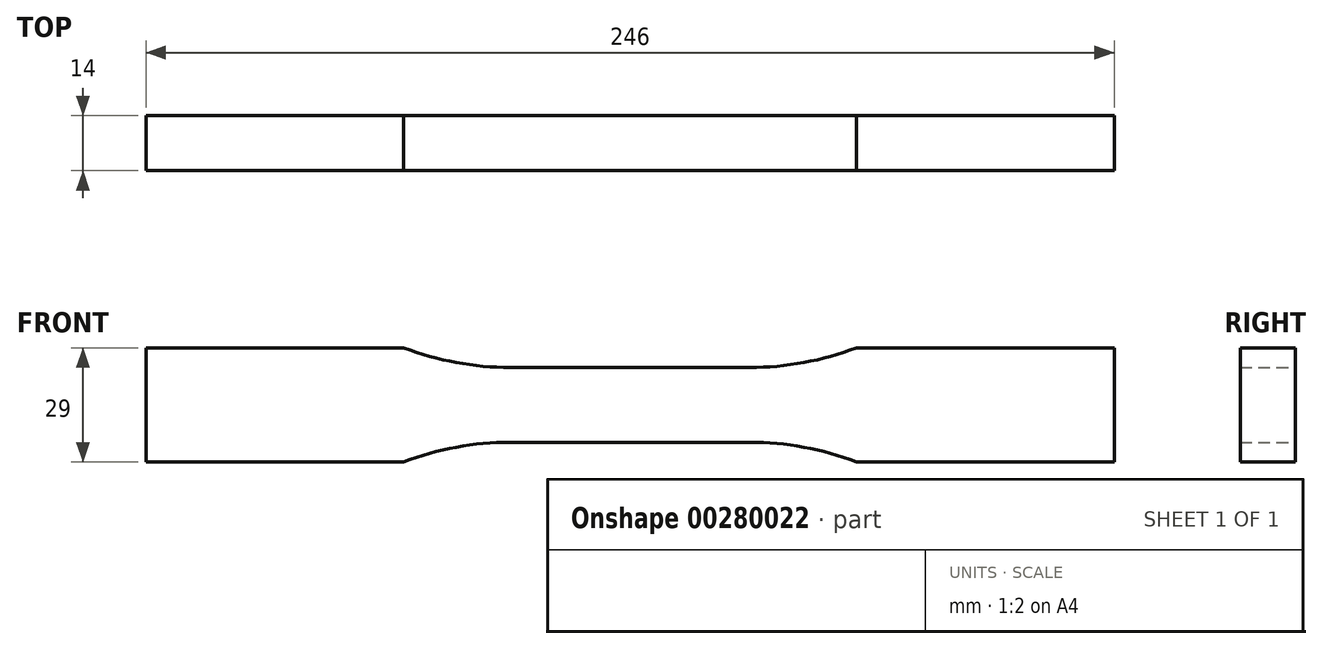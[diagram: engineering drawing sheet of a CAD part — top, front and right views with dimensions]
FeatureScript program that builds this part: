
annotation { "Feature Type Name" : "Feature", "Feature Type Description" : "" }
export const myFeature = defineFeature(function(context is Context, id is Id, definition is map)
    precondition{}
    {
        {
            var Q0;
            Q0=qCreatedBy(makeId("Front.planeOp"),FACE);
            var sketch = newSketch(context, id + "F0", { "sketchPlane" : qUnion([Q0])});
            skLineSegment(sketch, "E0", {"start": v(0, 9.5) * mm, "end": v(30.39, 9.5) * mm});
            skArc(sketch, "E1", {"start": v(30.39, 9.5) * mm, "mid": v(44.17, 10.76) * mm, "end": v(57.5, 14.5) * mm});
            skLineSegment(sketch, "E2", {"start": v(57.5, 14.5) * mm, "end": v(123, 14.5) * mm});
            skLineSegment(sketch, "E3", {"start": v(123, 14.5) * mm, "end": v(123, 0) * mm});
            skLineSegment(sketch, "E4.MirrorCS", {"start": v(0, -9.5) * mm, "end": v(30.39, -9.5) * mm});
            skLineSegment(sketch, "E5.MirrorCS", {"start": v(123, -14.5) * mm, "end": v(123, 0) * mm});
            skLineSegment(sketch, "E6.MirrorCS", {"start": v(57.5, -14.5) * mm, "end": v(123, -14.5) * mm});
            skArc(sketch, "E7.MirrorCS", {"start": v(30.39, -9.5) * mm, "mid": v(44.17, -10.76) * mm, "end": v(57.5, -14.5) * mm});
            skArc(sketch, "E8.MirrorCS", {"start": v(-30.39, -9.5) * mm, "mid": v(-44.17, -10.76) * mm, "end": v(-57.5, -14.5) * mm});
            skLineSegment(sketch, "E9.MirrorCS", {"start": v(-57.5, -14.5) * mm, "end": v(-123, -14.5) * mm});
            skArc(sketch, "E10.MirrorCS", {"start": v(-30.39, 9.5) * mm, "mid": v(-44.17, 10.76) * mm, "end": v(-57.5, 14.5) * mm});
            skLineSegment(sketch, "E11.MirrorCS", {"start": v(-57.5, 14.5) * mm, "end": v(-123, 14.5) * mm});
            skLineSegment(sketch, "E12.MirrorCS", {"start": v(-123, -14.5) * mm, "end": v(-123, 0) * mm});
            skLineSegment(sketch, "E13.MirrorCS", {"start": v(0, -9.5) * mm, "end": v(-30.39, -9.5) * mm});
            skLineSegment(sketch, "E14.MirrorCS", {"start": v(-123, 14.5) * mm, "end": v(-123, 0) * mm});
            skLineSegment(sketch, "E15.MirrorCS", {"start": v(0, 9.5) * mm, "end": v(-30.39, 9.5) * mm});
            skSolve(sketch);
        }
        {
            var Q0;
            Q0 = qSketchRegion(id + "F0", true);
            extrude(context, id + "F1", {"entities" : qUnion([Q0]), "endBound" : BoundingType.SYMMETRIC, "depth" : 14 * mm});
        }
    });
